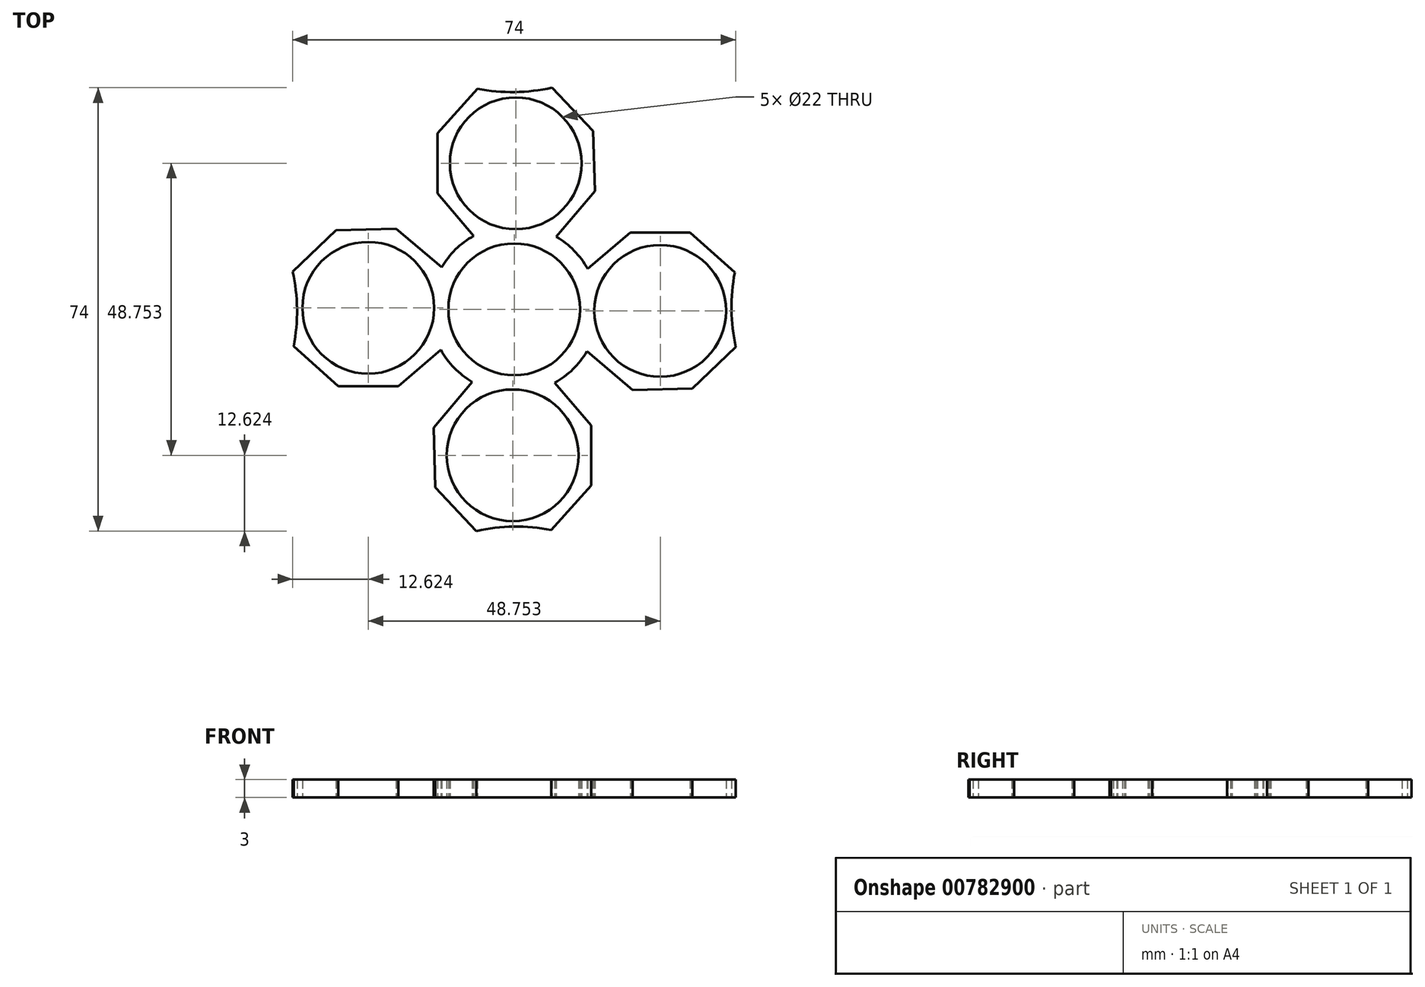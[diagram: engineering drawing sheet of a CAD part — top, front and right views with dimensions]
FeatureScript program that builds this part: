
annotation { "Feature Type Name" : "Feature", "Feature Type Description" : "" }
export const myFeature = defineFeature(function(context is Context, id is Id, definition is map)
    precondition{}
    {
        {
            var Q0;
            Q0=qCreatedBy(makeId("Top.planeOp"),FACE);
            var sketch = newSketch(context, id + "F0", { "sketchPlane" : qUnion([Q0])});
            skArc(sketch, "E0", {"start": v(7.78, 7.78) * mm, "mid": v(0, 11) * mm, "end": v(-7.78, 7.78) * mm});
            skCircle(sketch, "E1", {"center": v(0.26, 24.38) * mm, "radius": 11 * mm});
            skArc(sketch, "E2", {"start": v(9.9, 9.9) * mm, "mid": v(8.53, 11.1) * mm, "end": v(7.01, 12.12) * mm});
            skArc(sketch, "E3.trimOffspring", {"start": v(-6.76, 12.26) * mm, "mid": v(-8.41, 11.2) * mm, "end": v(-9.9, 9.9) * mm});
            skLineSegment(sketch, "E4", {"start": v(-6.76, 12.26) * mm, "end": v(-12.82, 19.38) * mm});
            skLineSegment(sketch, "E5", {"start": v(-12.82, 19.38) * mm, "end": v(-12.82, 29.38) * mm});
            skLineSegment(sketch, "E6", {"start": v(-12.82, 29.38) * mm, "end": v(-6.15, 36.83) * mm});
            skLineSegment(sketch, "E7", {"start": v(7.01, 12.12) * mm, "end": v(13.47, 19.75) * mm});
            skLineSegment(sketch, "E8", {"start": v(13.47, 19.75) * mm, "end": v(13.18, 29.75) * mm});
            skLineSegment(sketch, "E9", {"start": v(13.18, 29.75) * mm, "end": v(6.3, 37) * mm});
            skArc(sketch, "E10", {"start": v(-6.15, 36.83) * mm, "mid": v(0.09, 36.27) * mm, "end": v(6.3, 37) * mm});
            skCircle(sketch, "E11.1.0", {"center": v(-24.38, 0.26) * mm, "radius": 11 * mm});
            skLineSegment(sketch, "E11.1.1", {"start": v(-29.75, 13.18) * mm, "end": v(-37, 6.3) * mm});
            skLineSegment(sketch, "E11.1.2", {"start": v(-19.75, 13.47) * mm, "end": v(-29.75, 13.18) * mm});
            skArc(sketch, "E11.1.3", {"start": v(-7.78, 7.78) * mm, "mid": v(-11, 0) * mm, "end": v(-7.78, -7.78) * mm});
            skLineSegment(sketch, "E11.1.4", {"start": v(-12.26, -6.76) * mm, "end": v(-19.38, -12.82) * mm});
            skLineSegment(sketch, "E11.1.5", {"start": v(-29.38, -12.82) * mm, "end": v(-36.83, -6.15) * mm});
            skLineSegment(sketch, "E11.1.6", {"start": v(-19.38, -12.82) * mm, "end": v(-29.38, -12.82) * mm});
            skArc(sketch, "E11.1.7", {"start": v(-36.83, -6.15) * mm, "mid": v(-36.27, 0.09) * mm, "end": v(-37, 6.3) * mm});
            skLineSegment(sketch, "E11.1.8", {"start": v(-12.12, 7.01) * mm, "end": v(-19.75, 13.47) * mm});
            skArc(sketch, "E11.1.9", {"start": v(-9.9, 9.9) * mm, "mid": v(-11.1, 8.53) * mm, "end": v(-12.12, 7.01) * mm});
            skArc(sketch, "E11.1.10", {"start": v(-12.26, -6.76) * mm, "mid": v(-11.2, -8.41) * mm, "end": v(-9.9, -9.9) * mm});
            skCircle(sketch, "E11.2.0", {"center": v(-0.26, -24.38) * mm, "radius": 11 * mm});
            skLineSegment(sketch, "E11.2.1", {"start": v(-13.18, -29.75) * mm, "end": v(-6.3, -37) * mm});
            skLineSegment(sketch, "E11.2.2", {"start": v(-13.47, -19.75) * mm, "end": v(-13.18, -29.75) * mm});
            skArc(sketch, "E11.2.3", {"start": v(-7.78, -7.78) * mm, "mid": v(0, -11) * mm, "end": v(7.78, -7.78) * mm});
            skLineSegment(sketch, "E11.2.4", {"start": v(6.76, -12.26) * mm, "end": v(12.82, -19.38) * mm});
            skLineSegment(sketch, "E11.2.5", {"start": v(12.82, -29.38) * mm, "end": v(6.15, -36.83) * mm});
            skLineSegment(sketch, "E11.2.6", {"start": v(12.82, -19.38) * mm, "end": v(12.82, -29.38) * mm});
            skArc(sketch, "E11.2.7", {"start": v(6.15, -36.83) * mm, "mid": v(-0.09, -36.27) * mm, "end": v(-6.3, -37) * mm});
            skLineSegment(sketch, "E11.2.8", {"start": v(-7.01, -12.12) * mm, "end": v(-13.47, -19.75) * mm});
            skArc(sketch, "E11.2.9", {"start": v(-9.9, -9.9) * mm, "mid": v(-8.53, -11.1) * mm, "end": v(-7.01, -12.12) * mm});
            skArc(sketch, "E11.2.10", {"start": v(6.76, -12.26) * mm, "mid": v(8.41, -11.2) * mm, "end": v(9.9, -9.9) * mm});
            skCircle(sketch, "E11.3.0", {"center": v(24.38, -0.26) * mm, "radius": 11 * mm});
            skLineSegment(sketch, "E11.3.1", {"start": v(29.75, -13.18) * mm, "end": v(37, -6.3) * mm});
            skLineSegment(sketch, "E11.3.2", {"start": v(19.75, -13.47) * mm, "end": v(29.75, -13.18) * mm});
            skArc(sketch, "E11.3.3", {"start": v(7.78, -7.78) * mm, "mid": v(11, 0) * mm, "end": v(7.78, 7.78) * mm});
            skLineSegment(sketch, "E11.3.4", {"start": v(12.26, 6.76) * mm, "end": v(19.38, 12.82) * mm});
            skLineSegment(sketch, "E11.3.5", {"start": v(29.38, 12.82) * mm, "end": v(36.83, 6.15) * mm});
            skLineSegment(sketch, "E11.3.6", {"start": v(19.38, 12.82) * mm, "end": v(29.38, 12.82) * mm});
            skArc(sketch, "E11.3.7", {"start": v(36.83, 6.15) * mm, "mid": v(36.27, -0.09) * mm, "end": v(37, -6.3) * mm});
            skLineSegment(sketch, "E11.3.8", {"start": v(12.12, -7.01) * mm, "end": v(19.75, -13.47) * mm});
            skArc(sketch, "E11.3.9", {"start": v(9.9, -9.9) * mm, "mid": v(11.1, -8.53) * mm, "end": v(12.12, -7.01) * mm});
            skArc(sketch, "E11.3.10", {"start": v(12.26, 6.76) * mm, "mid": v(11.2, 8.41) * mm, "end": v(9.9, 9.9) * mm});
            skSolve(sketch);
        }
        {
            var Q0;
            Q0 = qSketchRegion(id + "F0", true);
            extrude(context, id + "F1", {"entities" : qUnion([Q0]), "depth" : 3 * mm, "offsetDistance" : 25 * mm});
        }
    });
